# Revit family: IS_CerathermT25_A7201_BIM_DE
name_source: partatom
category: Plumbing Fixtures
units: mm (PartAtom-declared; Revit-internal decimal feet)

## family parameters
Always vertical = No
Cut with Voids When Loaded = No
OmniClass Number = 23.45.55.17
OmniClass Title = Mixing Faucets
Part Type = Normal
Room Calculation Point = No
Round Connector Dimension = Use Diameter
Shared = No
Work Plane-Based = No

## types (2) — shared parameters
Accessories = https://www.idealstandard.de
Afmetingen = 315 x 100 x 70 mm
AfstandsEenheid = millimeter
Afwerking = Chroom
Artikelnummer = A7201
Artikelomschrijving = Brausethermostat AP CERATHERM T25, Ausladung 88 mm, Chrom
Artikelreferentie = A7201AA
Auteur = Ideal Standrad
BIMObjectName = IS_IdealStandard_Shower Mixers_CerathermT25_A7201AA
BIMobject category = Taps & Mixers
BIMobject category code = sanitary-taps-mixers
BIMobject main category = Sanitary
BIMobject main category code = sanitary
BarCode = 4015413345712
Bedieningkraan = LEVERHANDLE
Bedieningkraanwerk = Lever
Beschrijvinggarantie = Fabrieksgarantie
BimObjectNaam = IS_IdealStandard_Shower Mixers_CerathermT25_A7201AA
Brand = Ideal Standard
Brand url = https://www.idealstandard.de
Breedte = 314.4617
CisternCapacity = 0.00 m³
Color = Chrome
ConnectionType = Plumbing
CurrencyUnit = £
CurrentRevision = 1
Description = Ceratherm T25 Thermostat Entry Handle  S connectors
Diepte = 100 mm  [stored 0.328084 ft]
Douchebak = No
DurationUnit = Years
DuurEenheid = Jaar
Edition number = 1
Eigenschappen = Thermostat  Entry Handle Mixer, S Connectors, Chrome Finish
ExpectedLife = 30
FaucetFunction = MIXED
FaucetOperation = LEVERHANDLE
FaucetType = PILLAR
Features = Thermostat  Entry Handle Mixer, S Connectors, Chrome Finish
Finish = Chrome
FlushRate = 0.00 m³
GTIN code = https://4015413345712
Garantieonderdelen = 5
Garantieunits = Jaar
HasGrabHandles = No
HasIntegralShutOffDevice = No
HasTray = No
Heefthandvaten = No
Help = https://www.idealstandard.de
Hoogte = 70.2666130065918
Hulp = https://www.idealstandard.de
IFC Classification = Sanitary Terminal
IfcExportAs = IfcValveType
IfcExportType = FAUCET
Installatieinstructies = https://www.idealstandard.de
Installation instructions = https://www.idealstandard.de
InstallationInstructions = https://www.idealstandard.de
IsAutomaticFlush = No
IsBuiltIn = No
IsHighPressure = No
IsSingleFlush = No
Kleur = Chroom
LinearUnits = millimeters
MainColor = Chrome
MaintenanceInformation = https://www.idealstandard.de
Manufacturer = https://www.idealstandard.de
Manufacturer name = Ideal Standard
ManufacturerURL = https://www.idealstandard.de
Materiaal = Messing
Material = Brass
Material main = Brass
Merk = Ideal Standard
ModelNumber = A7201
ModelReference = A7201AA
Montageinstuctie = https://www.idealstandard.de
NBS Reference Code = 45-35-70/335
NBS Reference Description = Shower Mixers
Name = Shower Mixers_CerathermT25_A7201AA_IdealStandard
Nettogewicht = 1.1
NominalDepth = 100 mm  [stored 0.328084 ft]
NominalHeight = 70 mm
NominalWidth = 314 mm
OmniClass Code = 23-31 11 00
OmniClass Description = Faucets
OppervlakteEenheid = millimeters
Product Guid = 9c515542-caf2-4d66-bddc-14c83ec4a8d0
Product SKU = A7201
Product data url = https://bimobject.com
Product family = CERATHERM
Product group = Shower Mixer
Product name = A -Ceratherm T25 Thermostat Entry Handle  S connectors
Product url = https://www.idealstandard.de
ProductInformation = https://www.idealstandard.de
QR code = http://bimobject.com
Revisie = 1
SeatHasCover = No
Shape = Sculptured
Size = 315 x 100 x 70 mm
Space = Internal
SpareParts = http://spareparts-is.com
Technical description = https://www.idealstandard.de
Telefoonnummer = +49 (0) 228 521 0
TestPressure = 10Bar
Testdruk = 10Bar
Typekraanwerk = PILLAR
UNSPSC Code = 301815
URL = https://www.idealstandard.de
Uniclass 1.4 Code = L725111
Uniclass 1.4 Description = Mixer taps
Uniclass 2.0 Code = PR-35-06-82
Uniclass 2.0 Description = Shower Mixers
Uniclass 2015 Code = Pr_40_20_87_78
Uniclass 2015 Name = Shower manual water supply sets
Uniclass2015Beschrijving = Shower manual water supply sets
Uniclass2015Code = Pr_40_20_87_78
Uniclass2015Referentie = Pr_40_20_87_78
Uniclass2015Title = Shower manual water supply sets
Uniclass2015Version = v1.15
Urlproducent = https://www.idealstandard.de
Versie = 1
VolumeUnits = Litre
Volumeunits = liters
Vorm = Gebeeldhouwd
WarrantyDescription = Manufacturers Warranty
WarrantyDurationParts = 5
WarrantyDurationUnit = Years
WarrantyGuarantorParts = https://www.idealstandard.de
Wisselstukken = https://www.idealstandard.de
zero-valued in all types: BrutoGewicht, DrainSize, FlushingRate, GrootteAfvoergat, InletConnectionSize, Lengte, MaterialThickness, OutletConnectionSize, Overloop, SpilloverLevel, Vervangingskosten

## per-type parameters (varying)
| type | Model |
| A7201XG - CERATHEM RIM-MOUNTED T25 SHOWER MIXER EXPOSED - CHROME | A7201AA |
| A7201XG - CERATHEM RIM-MOUNTED T25 SHOWER MIXER EXPOSED - SILK BLACK | A7201XG |

note: [stored X ft] marks values corroborated as IEEE doubles in the binary element streams (Revit-internal decimal feet)

## geometry (parser evidence)
native form markers: Sweep x4
no freeform markers — native parametric forms only
